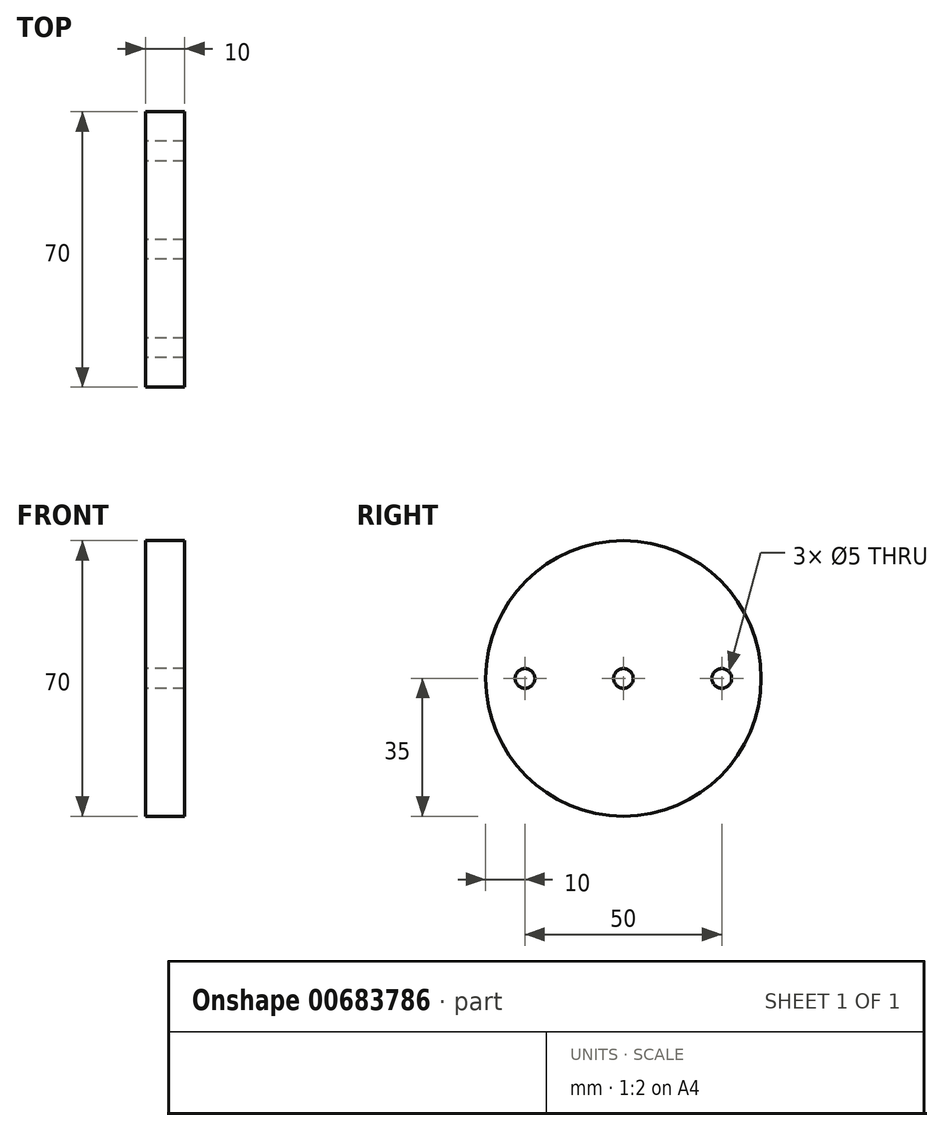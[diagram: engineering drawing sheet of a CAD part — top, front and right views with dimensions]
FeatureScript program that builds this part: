
annotation { "Feature Type Name" : "Feature", "Feature Type Description" : "" }
export const myFeature = defineFeature(function(context is Context, id is Id, definition is map)
    precondition{}
    {
        {
            var Q0;
            Q0=qCreatedBy(makeId("Right.planeOp"),FACE);
            var sketch = newSketch(context, id + "F0", { "sketchPlane" : qUnion([Q0])});
            skCircle(sketch, "E0", {"center": v(0, 0) * mm, "radius": 35 * mm});
            skLineSegment(sketch, "E1", {"start": v(0, 0) * mm, "end": v(25, 0) * mm});
            skCircle(sketch, "E2", {"center": v(25, 0) * mm, "radius": 2.5 * mm});
            skCircle(sketch, "E3.1.0.0", {"center": v(0, 0) * mm, "radius": 2.5 * mm});
            skCircle(sketch, "E3.2.0.0", {"center": v(-25, 0) * mm, "radius": 2.5 * mm});
            skLineSegment(sketch, "E3.direction1", {"start": v(25, 0) * mm, "end": v(0, 0) * mm, "construction": true});
            skSolve(sketch);
        }
        {
            var Q0;
            Q0=makeQuery(id+"F0.imprint","IMPRINT",FACE,{"disambiguationData":[TD([[makeQuery(id+"F0.imprint","IMPRINT",EDGE,{"derivedFrom":sQuery(id+"F0.wireOp",EDGE,"E0")}),1.0]])]});
            extrude(context, id + "F1", {"entities" : qUnion([Q0]), "endBound" : BoundingType.SYMMETRIC, "depth" : 10 * mm, "offsetDistance" : 25 * mm});
        }
    });
